# Revit family: Faucet_Single-American_Standard-Selectronic-7755.1xx_Series
name_source: partatom
category: Plumbing Fixtures
revit_build: Autodesk Revit 2014 (Build: 20130308_1515(x64)
units: mm (PartAtom-declared; Revit-internal decimal feet)

## types (9) — shared parameters
605XRCT Remote control adjusts setup parameters = No
605XTMV1070 Thermostatic mixing valve, 20" long = No
ADA Compliant = Yes
Assembly Code = D2020300
CW Connection = Yes
CWFU = 1.5
Connection Diameter = 3/8"
Default Elevation = 0"
Description = Nextgen Selectronic Integrated Proximity Lavatory Faucet Battery Powered. Vandal-resistant multi-laminar spray.
HW Connection = Yes
HWFU = 1.5
Height = 5 3/4"
Installation Type = Deck Mounted
Length = 6 7/8"
Manufacturer = American Standard
Material = Metal-American Standard-002-Polished Chrome
Plate Width = 2 1/2"
Price = Prices may vary. Please consult Manufacturer Representative for most up-to-date price list.
Revised Date = 6/11/2014
URL = http://www.americanstandard-us.com
Vent Connection = No
Waste Connection = No
Width = 1 7/8"
zero-valued in all types: WFU

## per-type parameters (varying)
| type | Actual Valve Water Flow | Deck Plate | Model | Plate Length |
| 7755.103 | 0 GPM | No | 7055.105 | 4" |
| 7755.105 | 1 GPM | No | 7755.105 | 4" |
| 7755.115 | 2 GPM | No | 7755.115 | 4" |
| 7755.103-4" | 0 GPM | Yes | 7055.105 | 4" |
| 7755.103-8" | 0 GPM | Yes | 7055.105 | 8" |
| 7755.105-4" | 1 GPM | Yes | 7755.105 | 4" |
| 7755.105-8" | 1 GPM | Yes | 7755.105 | 8" |
| 7755.115-4" | 2 GPM | Yes | 7755.115 | 4" |
| 7755.115-8" | 2 GPM | Yes | 7755.115 | 8" |

## geometry (parser evidence)
native form markers: Sweep x1
no freeform markers — native parametric forms only
